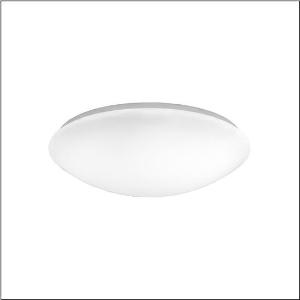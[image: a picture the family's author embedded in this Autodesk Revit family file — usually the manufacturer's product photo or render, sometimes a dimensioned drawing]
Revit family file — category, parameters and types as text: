
# Revit family: round_31_b_5pja212001a
name_source: partatom
category: Lighting Fixtures
units: mm (PartAtom-declared; Revit-internal decimal feet)

## family parameters
Cut with Voids When Loaded = No
Host = Face
Light Source = No
Part Type = Normal
Room Calculation Point = No
Round Connector Dimension = Use Diameter
Shared = No

## types (1)
- --- (1 x LED, 4700 lm, 39 W, 3000K)
    Apparent Load = 39 VA
    CIE Flux Codes = 42 71 89 88 100
    Color Rendering = 80
    Color Temperature = 3000K
    Default Elevation = 1800 mm
    Description = Round 31 B, wall and ceiling luminaire, primary optical cover: enclosure, of PMMA, light emission: direct distribution, primary light characteristic: symmetric, installation type: surface-mounted, LED, rated luminous flux: 4.700lm, luminous efficacy: 121lm/W, light colour: 830, colour temperature: 3000K, with terminal, 3+2-pole, max. 2.5mm², mains connection: 230V, AC, 50/60Hz, rated input power: 39W, luminaire housing, round, of steel, white, diameter: 464mm, height: 120mm, protection rating (complete): IP40, insulation class (complete): insulation class I (protective earthing), certification: CE, impact resistance: IK02, permissible operating ambient temperature: -20..+25°C, packaging unit: 1 piece
    Height = 120 mm
    Lamp = 1 x LED
    Lamp Light Flux = 4700 lm
    Lamp Power = 39 W
    Lamp count = 1
    Length = 464 mm
    Luminous efficacy = 121 lm/W
    Manufacturer = Siteco
    ModVariant = No
    Model = 5PJA212001A
    Mounting Place = Ceiling
    Mounting Type = Surface mounted
    Number of Poles = 1
    OnlyDefault = Yes
    Power Factor = 1
    Product Name = Round 31 B
    Product group = wall and ceiling luminaire
    ProductGroupID = 301
    Protection Class = Protection class I
    Protection Degree = IP 40
    RLX_Detail_Level = 1
    RLX_Emergency_Light_Flux = 0 lm
    RLX_Emergency_Type = 0
    RLX_Emergency_Type_DB = No
    RlxData = <blob elided: 13801 chars, md5=2578b59e>
    Socket = socket
    Standby Power = 0 W
    System Light Flux = 4700 lm
    System Power = 39 W
    Type Comments = factory setting: luminous flux: 100 % | (ON | ON | ON) | 1050 mA
    Type Image = l_1258313.jpg
    URL = http://relux.com
    VarID = @adj_013697
    Voltage = 0 V
    Weight = 0.00 kg
    Width = 0 mm  [stored 0 ft]

note: [stored X ft] marks values corroborated as IEEE doubles in the binary element streams (Revit-internal decimal feet)

## geometry (parser evidence)
native form markers: Sweep x13
no freeform markers — native parametric forms only
